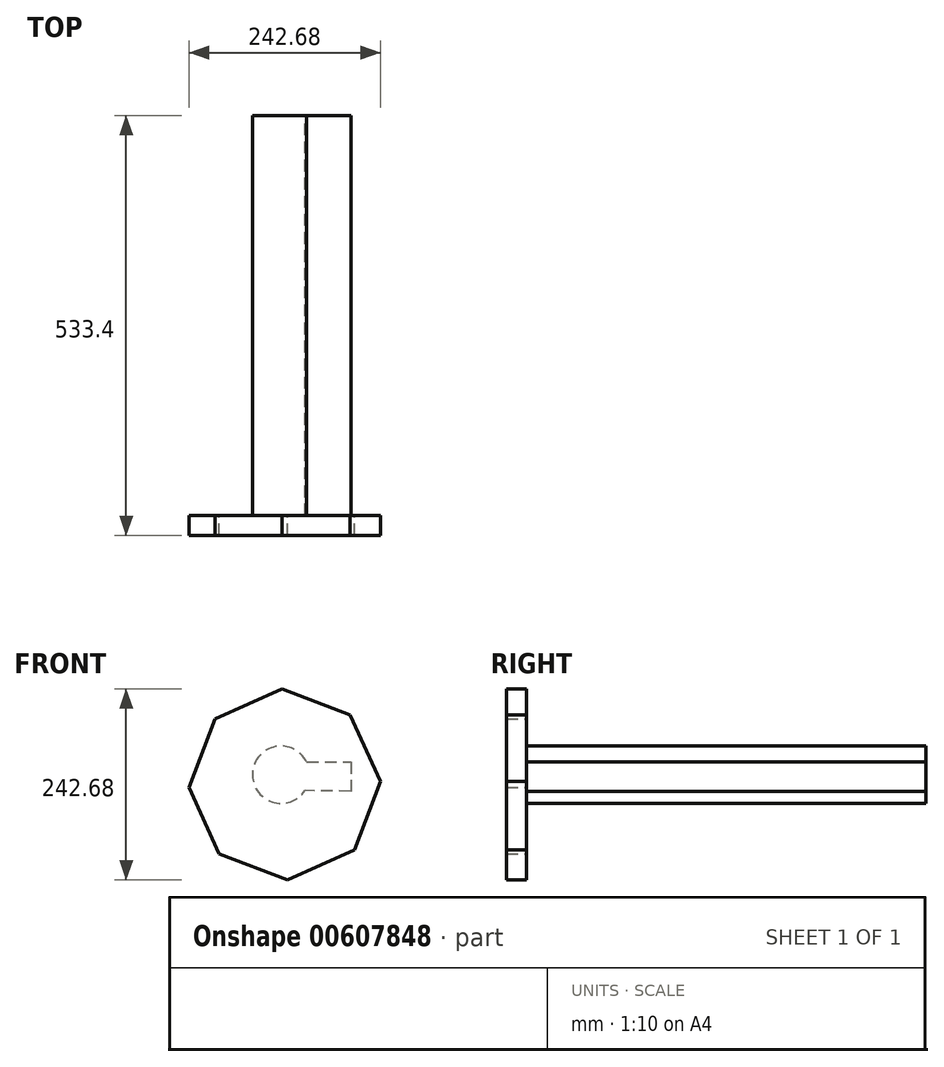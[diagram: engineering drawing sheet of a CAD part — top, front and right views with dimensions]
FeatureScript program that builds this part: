
annotation { "Feature Type Name" : "Feature", "Feature Type Description" : "" }
export const myFeature = defineFeature(function(context is Context, id is Id, definition is map)
    precondition{}
    {
        {
            var Q0;
            Q0=qCreatedBy(makeId("Front.planeOp"),FACE);
            var sketch = newSketch(context, id + "F0", { "sketchPlane" : qUnion([Q0])});
            skArc(sketch, "E0", {"start": v(32.6, 16.07) * mm, "mid": v(-36.27, 2.3) * mm, "end": v(30.3, -20.08) * mm});
            skLineSegment(sketch, "E1", {"start": v(32.6, 16.07) * mm, "end": v(88.64, 16.07) * mm});
            skLineSegment(sketch, "E2", {"start": v(88.64, 16.07) * mm, "end": v(88.64, -21.14) * mm});
            skLineSegment(sketch, "E3", {"start": v(88.64, -21.14) * mm, "end": v(30.3, -20.08) * mm});
            skSolve(sketch);
        }
        {
            var Q0;
            Q0 = qSketchRegion(id + "F0", true);
            var Q1;
            Q1=sQuery(id+"F0.wireOp",EDGE,"E3");
            var Q2;
            Q2=sQuery(id+"F0.wireOp",EDGE,"E2");
            var Q3;
            Q3=sQuery(id+"F0.wireOp",EDGE,"E1");
            var Q4;
            Q4=sQuery(id+"F0.wireOp",EDGE,"E0");
            extrude(context, id + "F1", {"entities" : qUnion([Q0]), "surfaceEntities" : qUnion([Q1, Q2, Q3, Q4]), "depth" : 508 * mm, "offsetDistance" : 25.4 * mm});
        }
        {
            var Q0;
            Q0=makeQuery(id+"F1.opExtrude","CAP_FACE",FACE,{"disambiguationData":[OSD([sQuery(id+"F0.wireOp",EDGE,"E0"),sQuery(id+"F0.wireOp",EDGE,"E1"),sQuery(id+"F0.wireOp",EDGE,"E2"),sQuery(id+"F0.wireOp",EDGE,"E3")])],"isStart":false});
            cPlane(context, id + "F2", {"entities" : qUnion([Q0]), "cplaneType" : CPlaneType.OFFSET, "offset" : 0 * mm, "width" : 152.4 * mm, "height" : 152.4 * mm});
        }
        {
            var Q0;
            Q0=qCreatedBy(id+"F2.planeOp",FACE);
            var sketch = newSketch(context, id + "F3", { "sketchPlane" : qUnion([Q0])});
            skCircle(sketch, "E4.cCircle", {"center": v(4.73, -12.38) * mm, "radius": 112.16 * mm, "construction": true});
            skLineSegment(sketch, "E4.0", {"start": v(8.46, -133.72) * mm, "end": v(-78.44, -100.82) * mm});
            skLineSegment(sketch, "E4.1", {"start": v(-78.44, -100.82) * mm, "end": v(-116.61, -16.1) * mm});
            skLineSegment(sketch, "E4.2", {"start": v(-116.61, -16.1) * mm, "end": v(-83.71, 70.79) * mm});
            skLineSegment(sketch, "E4.3", {"start": v(-83.71, 70.79) * mm, "end": v(1, 108.96) * mm});
            skLineSegment(sketch, "E4.4", {"start": v(1, 108.96) * mm, "end": v(87.9, 76.06) * mm});
            skLineSegment(sketch, "E4.5", {"start": v(87.9, 76.06) * mm, "end": v(126.07, -8.65) * mm});
            skLineSegment(sketch, "E4.6", {"start": v(126.07, -8.65) * mm, "end": v(93.17, -95.54) * mm});
            skLineSegment(sketch, "E4.7", {"start": v(93.17, -95.54) * mm, "end": v(8.46, -133.72) * mm});
            skPoint(sketch, "E4.0.midPoint", {"position": v(-34.99, -117.27) * mm});
            skSolve(sketch);
        }
        {
            var Q0;
            Q0=makeQuery(id+"F3.imprint","IMPRINT",FACE,{"disambiguationData":[TD([[makeQuery(id+"F3.imprint","IMPRINT",EDGE,{"derivedFrom":sQuery(id+"F3.wireOp",EDGE,"E4.0")}),-1.0]])]});
            extrude(context, id + "F4", {"entities" : qUnion([Q0]), "depth" : 25.4 * mm, "offsetDistance" : 25.4 * mm});
        }
    });
